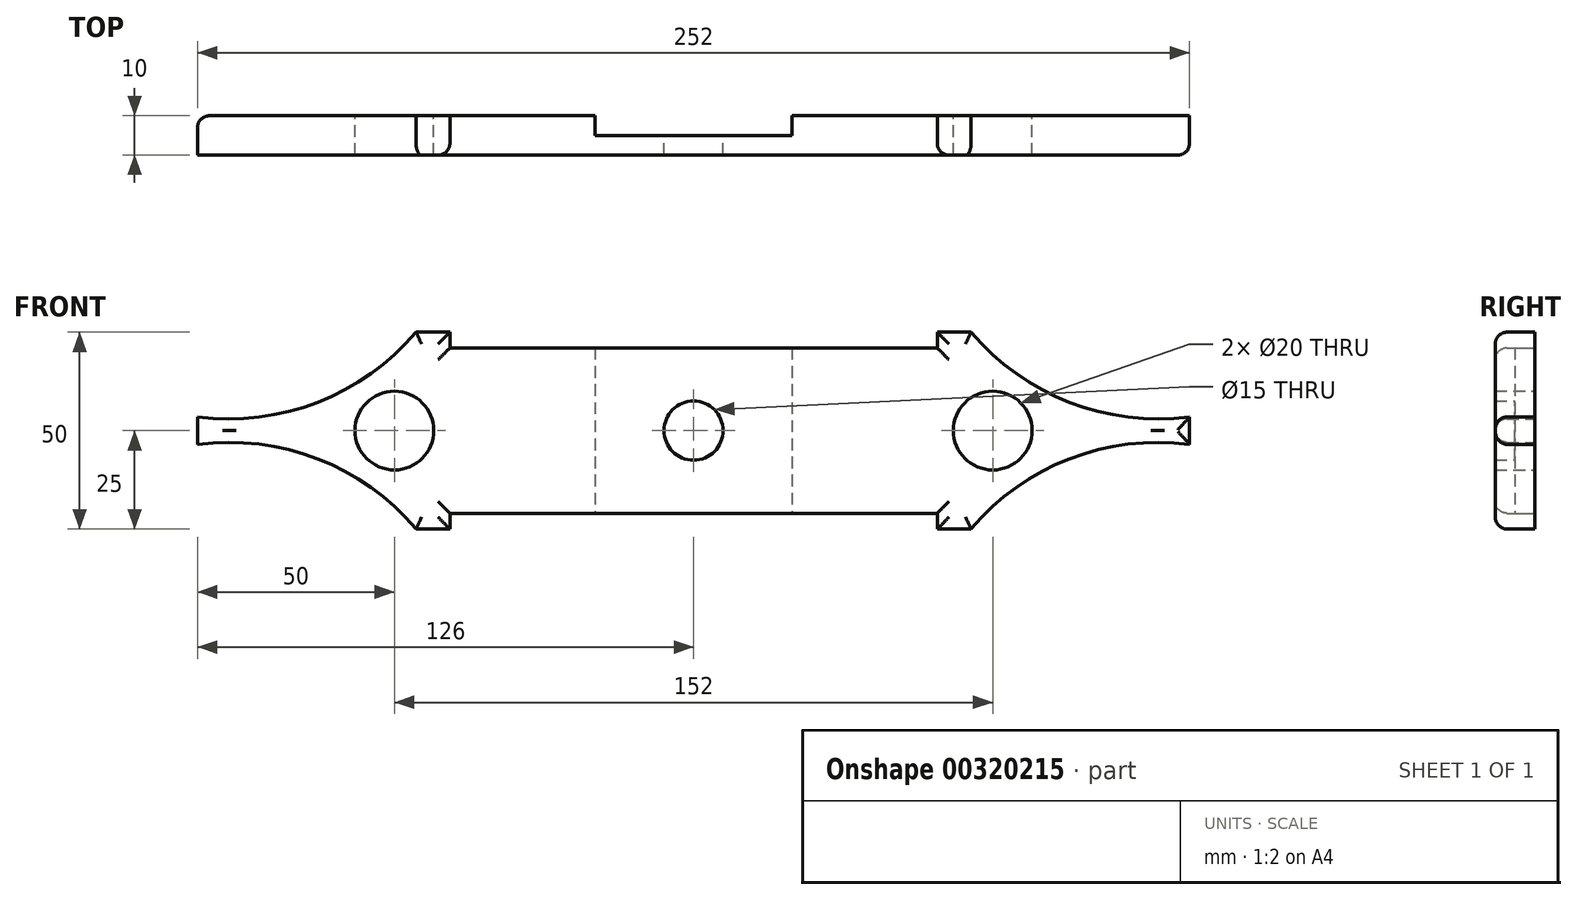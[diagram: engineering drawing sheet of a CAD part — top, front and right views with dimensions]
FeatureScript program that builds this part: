
annotation { "Feature Type Name" : "Feature", "Feature Type Description" : "" }
export const myFeature = defineFeature(function(context is Context, id is Id, definition is map)
    precondition{}
    {
        {
            var Q0;
            Q0=qCreatedBy(makeId("Front.planeOp"),FACE);
            var sketch = newSketch(context, id + "F0", { "sketchPlane" : qUnion([Q0])});
            skArc(sketch, "E0", {"start": v(70.5, 25) * mm, "mid": v(95.5, 7.17) * mm, "end": v(126, 3.5) * mm});
            skLineSegment(sketch, "E1", {"start": v(70.5, 25) * mm, "end": v(61.9, 25) * mm});
            skLineSegment(sketch, "E2", {"start": v(61.9, 25) * mm, "end": v(61.9, 21) * mm});
            skArc(sketch, "E3.MirrorCS", {"start": v(70.5, -25) * mm, "mid": v(95.5, -7.17) * mm, "end": v(126, -3.5) * mm});
            skLineSegment(sketch, "E4.MirrorCS", {"start": v(61.9, -25) * mm, "end": v(61.9, -21) * mm});
            skLineSegment(sketch, "E5", {"start": v(126, 3.5) * mm, "end": v(126, -3.5) * mm});
            skLineSegment(sketch, "E6.MirrorCS", {"start": v(-61.9, -25) * mm, "end": v(-61.9, -21) * mm});
            skArc(sketch, "E7.MirrorCS", {"start": v(-70.5, -25) * mm, "mid": v(-95.5, -7.17) * mm, "end": v(-126, -3.5) * mm});
            skLineSegment(sketch, "E8.MirrorCS", {"start": v(-126, 3.5) * mm, "end": v(-126, -3.5) * mm});
            skArc(sketch, "E9.MirrorCS", {"start": v(-70.5, 25) * mm, "mid": v(-95.5, 7.17) * mm, "end": v(-126, 3.5) * mm});
            skLineSegment(sketch, "E10.MirrorCS", {"start": v(-70.5, 25) * mm, "end": v(-61.9, 25) * mm});
            skLineSegment(sketch, "E11.MirrorCS", {"start": v(-61.9, 25) * mm, "end": v(-61.9, 21) * mm});
            skLineSegment(sketch, "E12", {"start": v(-61.9, -21) * mm, "end": v(61.9, -21) * mm});
            skLineSegment(sketch, "E13", {"start": v(-61.9, 21) * mm, "end": v(61.9, 21) * mm});
            skPoint(sketch, "E14.orphan", {"position": v(-40.13, 0) * mm});
            skCircle(sketch, "E15", {"center": v(-76, 0) * mm, "radius": 10 * mm});
            skLineSegment(sketch, "E16", {"start": v(-70.5, -25) * mm, "end": v(-61.9, -25) * mm});
            skLineSegment(sketch, "E17", {"start": v(61.9, -25) * mm, "end": v(70.5, -25) * mm});
            skCircle(sketch, "E18", {"center": v(0, 0) * mm, "radius": 7.5 * mm});
            skCircle(sketch, "E19", {"center": v(76, 0) * mm, "radius": 10 * mm});
            skSolve(sketch);
        }
        {
            var Q0;
            Q0 = qSketchRegion(id + "F0", true);
            extrude(context, id + "F1", {"entities" : qUnion([Q0]), "depth" : 10 * mm});
        }
        {
            var Q0;
            Q0=makeQuery(id+"F1.opExtrude","CAP_FACE",FACE,{"disambiguationData":[OSD([sQuery(id+"F0.wireOp",EDGE,"E0"),sQuery(id+"F0.wireOp",EDGE,"E1"),sQuery(id+"F0.wireOp",EDGE,"E2"),sQuery(id+"F0.wireOp",EDGE,"E3.MirrorCS"),sQuery(id+"F0.wireOp",EDGE,"E4.MirrorCS"),sQuery(id+"F0.wireOp",EDGE,"E5"),sQuery(id+"F0.wireOp",EDGE,"E6.MirrorCS"),sQuery(id+"F0.wireOp",EDGE,"E7.MirrorCS"),sQuery(id+"F0.wireOp",EDGE,"E8.MirrorCS"),sQuery(id+"F0.wireOp",EDGE,"E9.MirrorCS"),sQuery(id+"F0.wireOp",EDGE,"E10.MirrorCS"),sQuery(id+"F0.wireOp",EDGE,"E11.MirrorCS"),sQuery(id+"F0.wireOp",EDGE,"E12"),sQuery(id+"F0.wireOp",EDGE,"E13"),sQuery(id+"F0.wireOp",EDGE,"E15"),sQuery(id+"F0.wireOp",EDGE,"E16"),sQuery(id+"F0.wireOp",EDGE,"E17"),sQuery(id+"F0.wireOp",EDGE,"E18"),sQuery(id+"F0.wireOp",EDGE,"E19")])],"isStart":true});
            var sketch = newSketch(context, id + "F2", { "sketchPlane" : qUnion([Q0])});
            skLineSegment(sketch, "E20", {"start": v(-25, 21) * mm, "end": v(-25, -21) * mm});
            skLineSegment(sketch, "E21", {"start": v(25, 21) * mm, "end": v(25, -21) * mm});
            skSolve(sketch);
        }
        {
            var Q0;
            {var subQ0=sQuery(id+"F2.wireOp",EDGE,"E20");Q0=makeQuery(id+"F2.imprint","IMPRINT",FACE,{"disambiguationData":[TD([[makeQuery(id+"F2.imprint","IMPRINT",EDGE,{"derivedFrom":subQ0}),1.0]])]});}
            extrude(context, id + "F3", {"entities" : qUnion([Q0]), "operationType" : NewBodyOperationType.REMOVE, "oppositeDirection" : true, "depth" : 5 * mm});
        }
        {
            var Q0;
            Q0=makeQuery(id+"F1.opExtrude","CAP_EDGE",EDGE,{"disambiguationData":[OSD([sQuery(id+"F0.wireOp",EDGE,"E12")])],"isStart":false});
            var Q1;
            Q1=makeQuery(id+"F1.opExtrude","CAP_EDGE",EDGE,{"disambiguationData":[OSD([sQuery(id+"F0.wireOp",EDGE,"E4.MirrorCS")])],"isStart":false});
            var Q2;
            Q2=makeQuery(id+"F1.opExtrude","CAP_EDGE",EDGE,{"disambiguationData":[OSD([sQuery(id+"F0.wireOp",EDGE,"E3.MirrorCS")])],"isStart":false});
            var Q3;
            Q3=makeQuery(id+"F1.opExtrude","CAP_EDGE",EDGE,{"disambiguationData":[OSD([sQuery(id+"F0.wireOp",EDGE,"E17")])],"isStart":false});
            var Q4;
            Q4=makeQuery(id+"F1.opExtrude","CAP_EDGE",EDGE,{"disambiguationData":[OSD([sQuery(id+"F0.wireOp",EDGE,"E5")])],"isStart":false});
            var Q5;
            Q5=makeQuery(id+"F1.opExtrude","CAP_EDGE",EDGE,{"disambiguationData":[OSD([sQuery(id+"F0.wireOp",EDGE,"E0")])],"isStart":false});
            var Q6;
            Q6=makeQuery(id+"F1.opExtrude","CAP_EDGE",EDGE,{"disambiguationData":[OSD([sQuery(id+"F0.wireOp",EDGE,"E1")])],"isStart":false});
            var Q7;
            Q7=makeQuery(id+"F1.opExtrude","CAP_EDGE",EDGE,{"disambiguationData":[OSD([sQuery(id+"F0.wireOp",EDGE,"E2")])],"isStart":false});
            var Q8;
            Q8=makeQuery(id+"F1.opExtrude","CAP_EDGE",EDGE,{"disambiguationData":[OSD([sQuery(id+"F0.wireOp",EDGE,"E13")])],"isStart":false});
            var Q9;
            Q9=makeQuery(id+"F1.opExtrude","CAP_EDGE",EDGE,{"disambiguationData":[OSD([sQuery(id+"F0.wireOp",EDGE,"E11.MirrorCS")])],"isStart":false});
            var Q10;
            Q10=makeQuery(id+"F1.opExtrude","CAP_EDGE",EDGE,{"disambiguationData":[OSD([sQuery(id+"F0.wireOp",EDGE,"E10.MirrorCS")])],"isStart":false});
            var Q11;
            Q11=makeQuery(id+"F1.opExtrude","CAP_EDGE",EDGE,{"disambiguationData":[OSD([sQuery(id+"F0.wireOp",EDGE,"E9.MirrorCS")])],"isStart":false});
            var Q12;
            Q12=makeQuery(id+"F1.opExtrude","CAP_EDGE",EDGE,{"disambiguationData":[OSD([sQuery(id+"F0.wireOp",EDGE,"E6.MirrorCS")])],"isStart":false});
            var Q13;
            Q13=makeQuery(id+"F1.opExtrude","CAP_EDGE",EDGE,{"disambiguationData":[OSD([sQuery(id+"F0.wireOp",EDGE,"E7.MirrorCS")])],"isStart":false});
            var Q14;
            Q14=makeQuery(id+"F1.opExtrude","CAP_EDGE",EDGE,{"disambiguationData":[OSD([sQuery(id+"F0.wireOp",EDGE,"E16")])],"isStart":false});
            var Q15;
            Q15=makeQuery(id+"F1.opExtrude","CAP_EDGE",EDGE,{"disambiguationData":[OSD([sQuery(id+"F0.wireOp",EDGE,"E8.MirrorCS")])],"isStart":true});
            fillet(context, id + "F4", {"entities" : qUnion([Q0, Q1, Q2, Q3, Q4, Q5, Q6, Q7, Q8, Q9, Q10, Q11, Q12, Q13, Q14, Q15]), "radius" : 3 * mm, "tangentPropagation" : true, "allowEdgeOverflow" : false});
        }
    });
